# Revit family: 18-70-003 DN250
name_source: partatom
category: Pipe Accessories
units: mm (PartAtom-declared; Revit-internal decimal feet)

## family parameters
Always vertical = Yes
Cut with Voids When Loaded = No
Part Type = Valve - Breaks Into
Round Connector Dimension = Use Diameter
Shared = No
Work Plane-Based = No

## types (2) — shared parameters
1 = 1 mm  [stored 0.00328084 ft]
20 = 20 mm  [stored 0.0656168 ft]
27 = 27 mm  [stored 0.0885827 ft]
5 = 5 mm  [stored 0.0164042 ft]
50 = 50 mm  [stored 0.164042 ft]
Body_H = 285 mm  [stored 0.935039 ft]
Bore_R = 125 mm  [stored 0.410105 ft]
DN = 250 mm  [stored 0.82021 ft]
DN250_PN10 = 18-250-70-006
DN250_PN16 = 18-250-70-016
Description_ = AVK COMBI-CROSS, FLANGED, 4 OUTLETS, PN10/16
F = 14 mm  [stored 0.0459318 ft]
F1 = 20 mm  [stored 0.0656168 ft]
F2 = 65 mm  [stored 0.213255 ft]
F3 = 51 mm  [stored 0.167323 ft]
FL_R = 200 mm  [stored 0.656168 ft]
FL_T = 20 mm  [stored 0.0656168 ft]
H = 664 mm  [stored 2.17848 ft]
H1 = 371 mm  [stored 1.21719 ft]
H3 = 864 mm  [stored 2.83465 ft]
H3-H = 200 mm  [stored 0.656168 ft]
L = 960 mm  [stored 3.14961 ft]
L-L1 = 152 mm  [stored 0.498688 ft]
L1 = 656 mm  [stored 2.15223 ft]
L2 = 309 mm
L5 = 416 mm
L6 = 370 mm
L_half = 240 mm  [stored 0.787402 ft]
OD = 195 mm  [stored 0.639764 ft]
OD1 = 107 mm
OD2 = 118 mm
P1 = 464 mm  [stored 1.52231 ft]
Raised_R = 160 mm  [stored 0.524934 ft]
Raised_dis = 2 mm  [stored 0.00656168 ft]
Search_table = 18-70-003 DN250
URL_product_pages = https://www.avkvalves.com
W = 200 mm  [stored 0.656168 ft]
arc = 332 mm  [stored 1.08924 ft]
arc1 = 108 mm
arc2 = 216 mm  [stored 0.708661 ft]
body_dim1 = 185 mm  [stored 0.606955 ft]
main_dim1 = 156 mm
tp bore = 63 mm
zero-valued in all types: Default Elevation

## per-type parameters (varying)
| type | Dh |
| DN250_PN10 | 350 mm  [stored 1.14829 ft] |
| DN250_PN16 | 355 mm |

note: [stored X ft] marks values corroborated as IEEE doubles in the binary element streams (Revit-internal decimal feet)

## geometry (parser evidence)
native form markers: Sweep x6
no freeform markers — native parametric forms only
